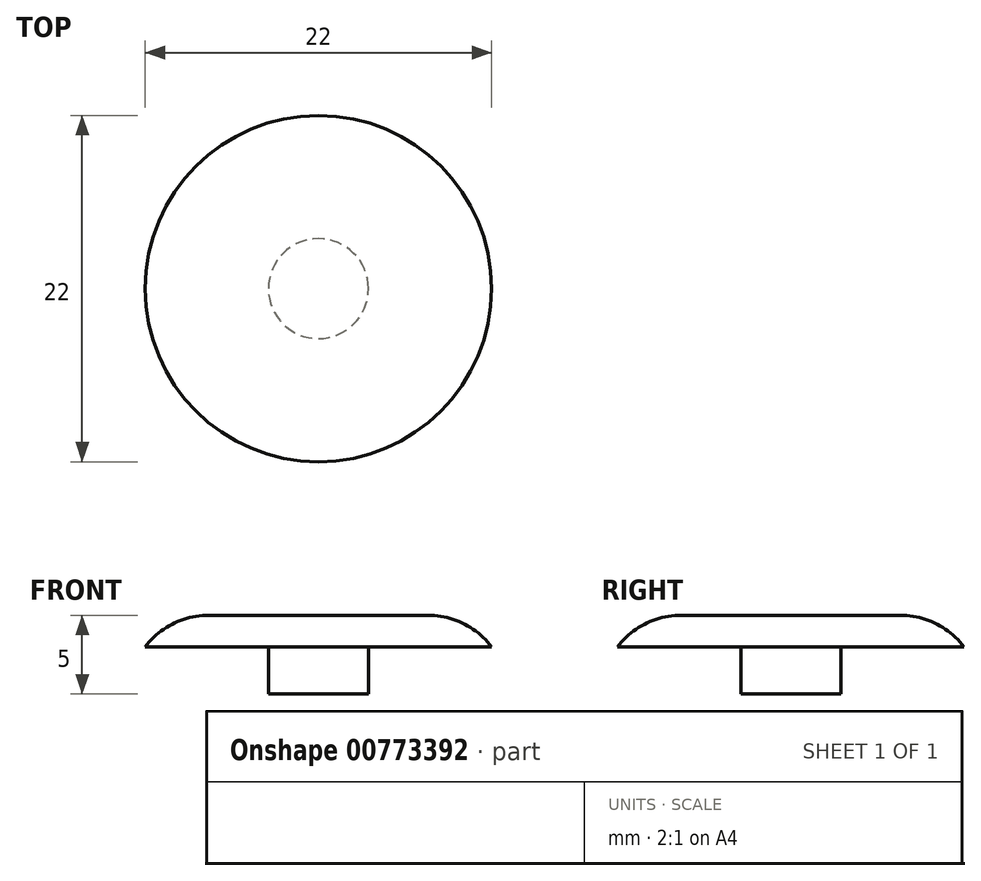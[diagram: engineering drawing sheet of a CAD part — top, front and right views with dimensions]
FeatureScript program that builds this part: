
annotation { "Feature Type Name" : "Feature", "Feature Type Description" : "" }
export const myFeature = defineFeature(function(context is Context, id is Id, definition is map)
    precondition{}
    {
        {
            var Q0;
            Q0=qCreatedBy(makeId("Top.planeOp"),FACE);
            var sketch = newSketch(context, id + "F0", { "sketchPlane" : qUnion([Q0])});
            skCircle(sketch, "E0", {"center": v(0, 0) * mm, "radius": 11 * mm});
            skSolve(sketch);
        }
        {
            var Q0;
            Q0=qCreatedBy(makeId("Top.planeOp"),FACE);
            var sketch = newSketch(context, id + "F1", { "sketchPlane" : qUnion([Q0])});
            skCircle(sketch, "E1", {"center": v(0, 0) * mm, "radius": 3.18 * mm});
            skSolve(sketch);
        }
        {
            var Q0;
            Q0=makeQuery(id+"F0.imprint","IMPRINT",FACE,{"disambiguationData":[TD([[makeQuery(id+"F0.imprint","IMPRINT",EDGE,{"derivedFrom":sQuery(id+"F0.wireOp",EDGE,"E0")}),1.0]])]});
            extrude(context, id + "F2", {"entities" : qUnion([Q0]), "depth" : 2 * mm, "offsetDistance" : 25.4 * mm});
        }
        {
            var Q0;
            Q0 = qSketchRegion(id + "F1", true);
            extrude(context, id + "F3", {"entities" : qUnion([Q0]), "operationType" : NewBodyOperationType.ADD, "oppositeDirection" : true, "depth" : 3 * mm, "offsetDistance" : 25.4 * mm});
        }
        {
            var Q0;
            Q0=makeQuery(id+"F2.opExtrude","CAP_EDGE",EDGE,{"disambiguationData":[OSD([sQuery(id+"F0.wireOp",EDGE,"E0")])],"isStart":false});
            fillet(context, id + "F4", {"entities" : qUnion([Q0]), "radius" : 5.08 * mm, "tangentPropagation" : true, "allowEdgeOverflow" : false});
        }
    });
